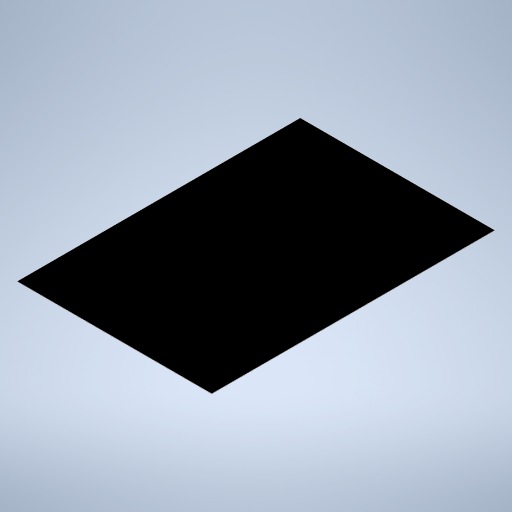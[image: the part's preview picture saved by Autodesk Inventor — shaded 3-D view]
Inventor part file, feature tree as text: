
AUTODESK INVENTOR PART (.ipt)
format: ipt  version: 2023 (Build 270158000, 158)  size: 214,016 bytes
history: native  units: mm
features: other x1, extrude x1, sketch x1
ambient origin geometry x8: Origin, YZ Plane, XZ Plane, XY Plane, X Axis, Y Axis, Z Axis, Center Point
bodies: Body1 (feature_tree)
feature tree (3):
  other  "ソリッド1"
  extrude  "押し出し1"  Depth=275.0mm
  sketch  "スケッチ1"
